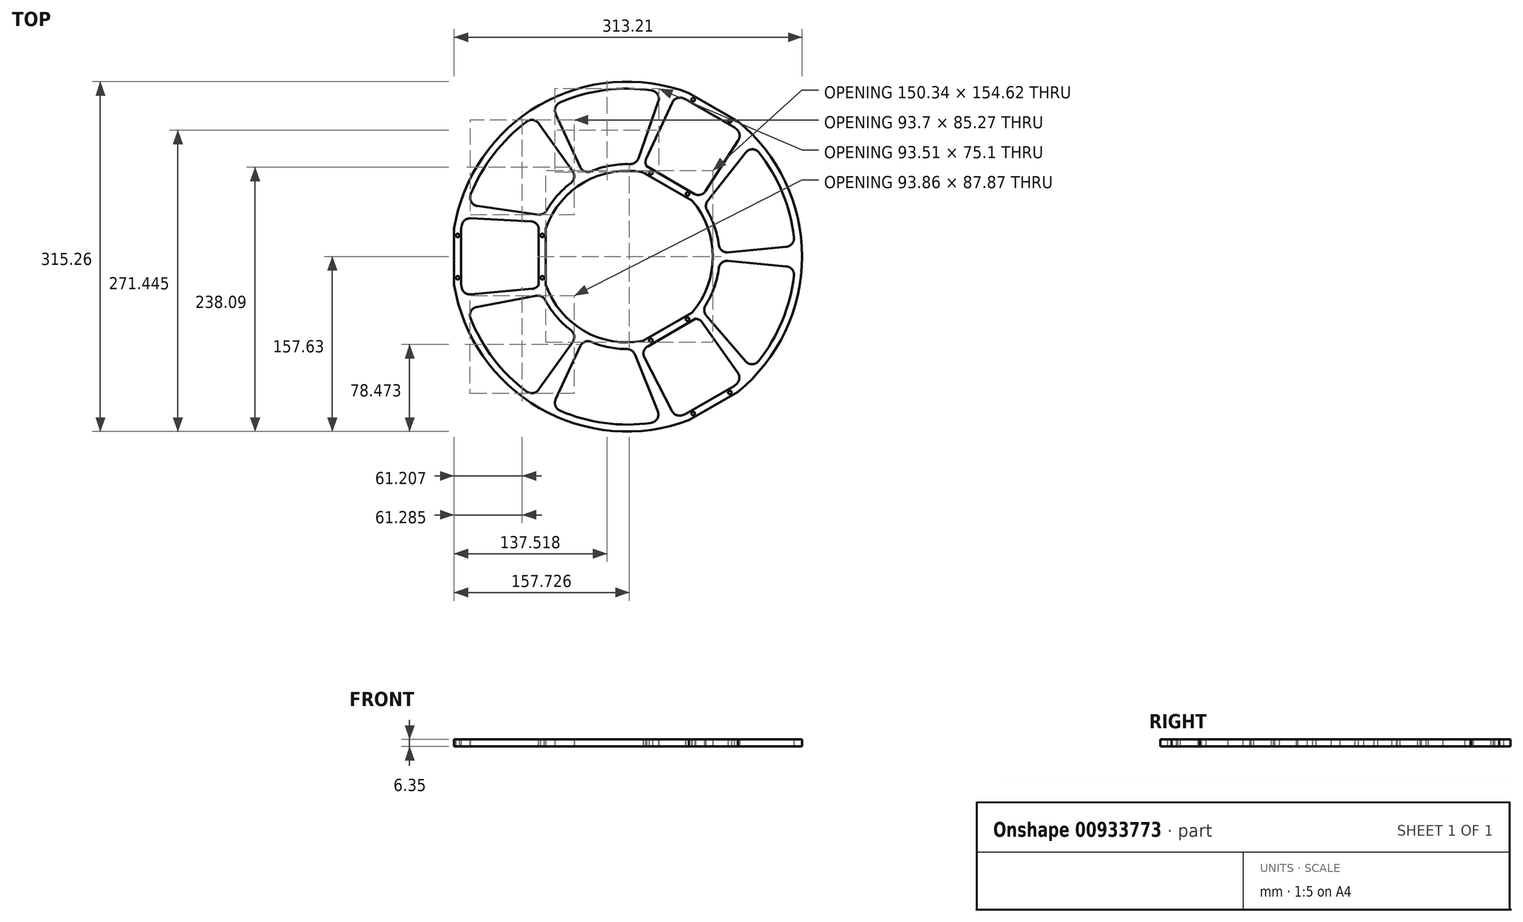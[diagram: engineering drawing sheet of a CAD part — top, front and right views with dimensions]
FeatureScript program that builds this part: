
annotation { "Feature Type Name" : "Feature", "Feature Type Description" : "" }
export const myFeature = defineFeature(function(context is Context, id is Id, definition is map)
    precondition{}
    {
        {
            var Q0;
            Q0=qCreatedBy(makeId("Top.planeOp"),FACE);
            var sketch = newSketch(context, id + "F0", { "sketchPlane" : qUnion([Q0])});
            skLineSegment(sketch, "E0", {"start": v(-79.38, 25.4) * mm, "end": v(-79.38, -25.4) * mm});
            skLineSegment(sketch, "E1", {"start": v(-79.38, -25.4) * mm, "end": v(-73.02, -25.4) * mm});
            skLineSegment(sketch, "E2", {"start": v(-73.02, -25.4) * mm, "end": v(-73.02, 25.4) * mm});
            skLineSegment(sketch, "E3", {"start": v(-73.02, 25.4) * mm, "end": v(-79.38, 25.4) * mm});
            skPoint(sketch, "E4", {"position": v(-79.38, 0) * mm});
            skPoint(sketch, "E5", {"position": v(-76.2, 25.4) * mm});
            skLineSegment(sketch, "E6.bottom", {"start": v(-149.22, 25.4) * mm, "end": v(-155.57, 25.4) * mm});
            skLineSegment(sketch, "E6.top", {"start": v(-149.22, -25.4) * mm, "end": v(-155.57, -25.4) * mm});
            skLineSegment(sketch, "E6.left", {"start": v(-149.22, 25.4) * mm, "end": v(-149.22, -25.4) * mm});
            skLineSegment(sketch, "E6.right", {"start": v(-155.57, 25.4) * mm, "end": v(-155.57, -25.4) * mm});
            skPoint(sketch, "E7", {"position": v(-152.4, 25.4) * mm});
            skCircle(sketch, "E8", {"center": v(0, 0) * mm, "radius": 77.32 * mm, "construction": true});
            skCircle(sketch, "E9", {"center": v(0, 0) * mm, "radius": 83.34 * mm, "construction": true});
            skCircle(sketch, "E10", {"center": v(0, 0) * mm, "radius": 151.37 * mm, "construction": true});
            skCircle(sketch, "E11", {"center": v(0, 0) * mm, "radius": 157.63 * mm, "construction": true});
            skCircle(sketch, "E12", {"center": v(-152.4, 19.05) * mm, "radius": 1.59 * mm});
            skCircle(sketch, "E13", {"center": v(-152.4, -19.05) * mm, "radius": 1.59 * mm});
            skCircle(sketch, "E14", {"center": v(-76.2, -19.05) * mm, "radius": 1.59 * mm});
            skCircle(sketch, "E15", {"center": v(-76.2, 19.05) * mm, "radius": 1.59 * mm});
            skCircle(sketch, "E16", {"center": v(0, 0) * mm, "radius": 33.02 * mm, "construction": true});
            skCircle(sketch, "E17", {"center": v(0, 0) * mm, "radius": 44.45 * mm, "construction": true});
            skSolve(sketch);
        }
        {
            var Q0;
            Q0 = qSketchRegion(id + "F0", true);
            extrude(context, id + "F1", {"entities" : qUnion([Q0]), "depth" : 6.35 * mm, "offsetDistance" : 25.4 * mm});
        }
        {
            var Q0;
            Q0=makeQuery(id+"F1.opExtrude","SWEPT_BODY",BODY,{"disambiguationData":[OSD([sQuery(id+"F0.wireOp",EDGE,"E6.bottom"),sQuery(id+"F0.wireOp",EDGE,"E6.top"),sQuery(id+"F0.wireOp",EDGE,"E6.left"),sQuery(id+"F0.wireOp",EDGE,"E6.right")])]});
            var Q1;
            Q1=makeQuery(id+"F1.opExtrude","SWEPT_BODY",BODY,{"disambiguationData":[OSD([sQuery(id+"F0.wireOp",EDGE,"E0"),sQuery(id+"F0.wireOp",EDGE,"E1"),sQuery(id+"F0.wireOp",EDGE,"E2"),sQuery(id+"F0.wireOp",EDGE,"E3")])]});
            var Q2;
            Q2=sQuery(id+"F0.wireOp",EDGE,"E8");
            circularPattern(context, id + "F2", {"operationType" : NewBodyOperationType.ADD, "entities" : qUnion([Q0, Q1]), "axis" : qUnion([Q2]), "angle" : 360 * degree, "instanceCount" : 3, "equalSpace" : true});
        }
        {
            var Q0;
            Q0=qCreatedBy(makeId("Top.planeOp"),FACE);
            var sketch = newSketch(context, id + "F3", { "sketchPlane" : qUnion([Q0])});
            skArc(sketch, "E18", {"start": v(14.52, 75.94) * mm, "mid": v(-38.66, 66.96) * mm, "end": v(-73.02, 25.4) * mm});
            skArc(sketch, "E19", {"start": v(17.7, 81.44) * mm, "mid": v(-41.67, 72.17) * mm, "end": v(-79.37, 25.4) * mm});
            skArc(sketch, "E20", {"start": v(52.62, 141.93) * mm, "mid": v(-75.69, 131.1) * mm, "end": v(-149.22, 25.4) * mm});
            skArc(sketch, "E21", {"start": v(55.8, 147.43) * mm, "mid": v(-78.82, 136.52) * mm, "end": v(-155.58, 25.4) * mm});
            skLineSegment(sketch, "E22", {"start": v(14.52, 75.94) * mm, "end": v(17.7, 81.44) * mm});
            skLineSegment(sketch, "E23", {"start": v(-73.02, 25.4) * mm, "end": v(-79.37, 25.4) * mm});
            skLineSegment(sketch, "E24", {"start": v(55.8, 147.43) * mm, "end": v(52.62, 141.93) * mm});
            skLineSegment(sketch, "E25", {"start": v(-155.58, 25.4) * mm, "end": v(-149.22, 25.4) * mm});
            skPoint(sketch, "E26", {"position": v(-75.69, 131.1) * mm});
            skPoint(sketch, "E27", {"position": v(-41.67, 72.17) * mm});
            skLineSegment(sketch, "E28", {"start": v(-75.69, 131.1) * mm, "end": v(-41.67, 72.17) * mm, "construction": true});
            skLineSegment(sketch, "E29", {"start": v(-83.78, 126.07) * mm, "end": v(-44.39, 70.53) * mm});
            skLineSegment(sketch, "E30", {"start": v(-38.9, 73.7) * mm, "end": v(-67.3, 135.6) * mm});
            skLineSegment(sketch, "E31", {"start": v(-147.33, 34.74) * mm, "end": v(-77.21, 31.37) * mm});
            skLineSegment(sketch, "E32", {"start": v(-143.9, 46.96) * mm, "end": v(-74.6, 37.16) * mm});
            skLineSegment(sketch, "E33", {"start": v(43.58, 144.96) * mm, "end": v(14.58, 82.06) * mm});
            skLineSegment(sketch, "E34", {"start": v(8.29, 82.93) * mm, "end": v(31.28, 148.1) * mm});
            skSolve(sketch);
        }
        {
            var Q0;
            Q0=makeQuery(id+"F3.imprint","IMPRINT",FACE,{"disambiguationData":[TD([[makeQuery(id+"F3.imprint","IMPRINT",EDGE,{"derivedFrom":sQuery(id+"F3.wireOp",EDGE,"E21")}),1.0]])]});
            var Q1;
            {var subQ0=sQuery(id+"F3.wireOp",EDGE,"E33");Q1=makeQuery(id+"F3.imprint","IMPRINT",FACE,{"disambiguationData":[TD([[makeQuery(id+"F3.imprint","IMPRINT",EDGE,{"derivedFrom":subQ0}),-1.0]])]});}
            var Q2;
            {var subQ0=sQuery(id+"F3.wireOp",EDGE,"E29");Q2=makeQuery(id+"F3.imprint","IMPRINT",FACE,{"disambiguationData":[TD([[makeQuery(id+"F3.imprint","IMPRINT",EDGE,{"derivedFrom":subQ0}),1.0]])]});}
            var Q3;
            {var subQ0=sQuery(id+"F3.wireOp",EDGE,"E31");Q3=makeQuery(id+"F3.imprint","IMPRINT",FACE,{"disambiguationData":[TD([[makeQuery(id+"F3.imprint","IMPRINT",EDGE,{"derivedFrom":subQ0}),1.0]])]});}
            var Q4;
            Q4=makeQuery(id+"F3.imprint","IMPRINT",FACE,{"disambiguationData":[TD([[makeQuery(id+"F3.imprint","IMPRINT",EDGE,{"derivedFrom":sQuery(id+"F3.wireOp",EDGE,"E18")}),-1.0]])]});
            extrude(context, id + "F4", {"entities" : qUnion([Q0, Q1, Q2, Q3, Q4]), "operationType" : NewBodyOperationType.ADD, "depth" : 6.35 * mm, "offsetDistance" : 25.4 * mm});
        }
        {
            var Q0;
            Q0=makeQuery(id+"F4.opExtrude","SWEPT_EDGE",EDGE,{"disambiguationData":[OSD([sQuery(id+"F3.wireOp",EDGE,"E20"),sQuery(id+"F3.wireOp",EDGE,"E29")])]});
            var Q1;
            Q1=makeQuery(id+"F4.opExtrude","SWEPT_EDGE",EDGE,{"disambiguationData":[OSD([sQuery(id+"F3.wireOp",EDGE,"E20"),sQuery(id+"F3.wireOp",EDGE,"E32")])]});
            var Q2;
            Q2=makeQuery(id+"F4.opExtrude","SWEPT_EDGE",EDGE,{"disambiguationData":[OSD([sQuery(id+"F3.wireOp",EDGE,"E19"),sQuery(id+"F3.wireOp",EDGE,"E32")])]});
            var Q3;
            Q3=makeQuery(id+"F4.opExtrude","SWEPT_EDGE",EDGE,{"disambiguationData":[OSD([sQuery(id+"F3.wireOp",EDGE,"E19"),sQuery(id+"F3.wireOp",EDGE,"E29")])]});
            var Q4;
            Q4=makeQuery(id+"F4.opExtrude","SWEPT_EDGE",EDGE,{"disambiguationData":[OSD([sQuery(id+"F3.wireOp",EDGE,"E19"),sQuery(id+"F3.wireOp",EDGE,"E30")])]});
            var Q5;
            Q5=makeQuery(id+"F4.opExtrude","SWEPT_EDGE",EDGE,{"disambiguationData":[OSD([sQuery(id+"F3.wireOp",EDGE,"E19"),sQuery(id+"F3.wireOp",EDGE,"E34")])]});
            var Q6;
            Q6=makeQuery(id+"F4.opExtrude","SWEPT_EDGE",EDGE,{"disambiguationData":[OSD([sQuery(id+"F3.wireOp",EDGE,"E20"),sQuery(id+"F3.wireOp",EDGE,"E34")])]});
            var Q7;
            Q7=makeQuery(id+"F4.opExtrude","SWEPT_EDGE",EDGE,{"disambiguationData":[OSD([sQuery(id+"F3.wireOp",EDGE,"E20"),sQuery(id+"F3.wireOp",EDGE,"E30")])]});
            var Q8;
            Q8=makeQuery(id+"F4.opExtrude","SWEPT_EDGE",EDGE,{"disambiguationData":[OSD([sQuery(id+"F3.wireOp",EDGE,"E20"),sQuery(id+"F3.wireOp",EDGE,"E31")])]});
            var Q9;
            Q9=makeQuery(id+"F4.opExtrude","SWEPT_EDGE",EDGE,{"disambiguationData":[OSD([sQuery(id+"F3.wireOp",EDGE,"E19"),sQuery(id+"F3.wireOp",EDGE,"E31")])]});
            var Q10;
            Q10=makeQuery(id+"F4.opExtrude","SWEPT_EDGE",EDGE,{"disambiguationData":[OSD([sQuery(id+"F3.wireOp",EDGE,"E20"),sQuery(id+"F3.wireOp",EDGE,"E33")])]});
            var Q11;
            Q11=makeQuery(id+"F4.opExtrude","SWEPT_EDGE",EDGE,{"disambiguationData":[OSD([sQuery(id+"F3.wireOp",EDGE,"E19"),sQuery(id+"F3.wireOp",EDGE,"E33")])]});
            fillet(context, id + "F5", {"entities" : qUnion([Q0, Q1, Q2, Q3, Q4, Q5, Q6, Q7, Q8, Q9, Q10, Q11]), "radius" : 7.62 * mm, "tangentPropagation" : true, "allowEdgeOverflow" : false});
        }
        {
            var Q0;
            Q0=makeQuery(id+"F5.opFillet","BLEND_EDGE",EDGE,{"blendedFrom":[makeQuery(id+"F4.opExtrude","SWEPT_EDGE",EDGE,{"disambiguationData":[OSD([sQuery(id+"F3.wireOp",EDGE,"E19"),sQuery(id+"F3.wireOp",EDGE,"E33")])]}),makeQuery(id+"F2.opPattern","COPY",FACE,{"derivedFrom":makeQuery(id+"F1.opExtrude","SWEPT_FACE",FACE,{"disambiguationData":[OSD([sQuery(id+"F0.wireOp",EDGE,"E0")])]}),"instanceName":"5"})],"blendedInto":[makeQuery(id+"F2.opPattern","COPY",FACE,{"derivedFrom":makeQuery(id+"F1.opExtrude","SWEPT_FACE",FACE,{"disambiguationData":[OSD([sQuery(id+"F0.wireOp",EDGE,"E0")])]}),"instanceName":"5"})]});
            var Q1;
            Q1=makeQuery(id+"F5.opFillet","BLEND_EDGE",EDGE,{"blendedFrom":[makeQuery(id+"F4.opExtrude","SWEPT_EDGE",EDGE,{"disambiguationData":[OSD([sQuery(id+"F3.wireOp",EDGE,"E20"),sQuery(id+"F3.wireOp",EDGE,"E33")])]}),makeQuery(id+"F2.opPattern","COPY",FACE,{"derivedFrom":makeQuery(id+"F1.opExtrude","SWEPT_FACE",FACE,{"disambiguationData":[OSD([sQuery(id+"F0.wireOp",EDGE,"E6.left")])]}),"instanceName":"5"})],"blendedInto":[makeQuery(id+"F2.opPattern","COPY",FACE,{"derivedFrom":makeQuery(id+"F1.opExtrude","SWEPT_FACE",FACE,{"disambiguationData":[OSD([sQuery(id+"F0.wireOp",EDGE,"E6.left")])]}),"instanceName":"5"})]});
            var Q2;
            Q2=makeQuery(id+"F5.opFillet","BLEND_EDGE",EDGE,{"blendedFrom":[makeQuery(id+"F4.opExtrude","SWEPT_EDGE",EDGE,{"disambiguationData":[OSD([sQuery(id+"F3.wireOp",EDGE,"E19"),sQuery(id+"F3.wireOp",EDGE,"E31")])]}),makeQuery(id+"F1.opExtrude","SWEPT_FACE",FACE,{"disambiguationData":[OSD([sQuery(id+"F0.wireOp",EDGE,"E0")])]})],"blendedInto":[makeQuery(id+"F1.opExtrude","SWEPT_FACE",FACE,{"disambiguationData":[OSD([sQuery(id+"F0.wireOp",EDGE,"E0")])]})]});
            var Q3;
            Q3=makeQuery(id+"F5.opFillet","BLEND_EDGE",EDGE,{"blendedFrom":[makeQuery(id+"F4.opExtrude","SWEPT_EDGE",EDGE,{"disambiguationData":[OSD([sQuery(id+"F3.wireOp",EDGE,"E20"),sQuery(id+"F3.wireOp",EDGE,"E31")])]}),makeQuery(id+"F1.opExtrude","SWEPT_FACE",FACE,{"disambiguationData":[OSD([sQuery(id+"F0.wireOp",EDGE,"E6.left")])]})],"blendedInto":[makeQuery(id+"F1.opExtrude","SWEPT_FACE",FACE,{"disambiguationData":[OSD([sQuery(id+"F0.wireOp",EDGE,"E6.left")])]})]});
            var Q4;
            {var subQ0=sQuery(id+"F3.wireOp",EDGE,"E19");Q4=makeQuery(id+"F5.opFillet","BLEND_EDGE",EDGE,{"blendedFrom":[makeQuery(id+"F4.opExtrude","SWEPT_EDGE",EDGE,{"disambiguationData":[OSD([subQ0,sQuery(id+"F3.wireOp",EDGE,"E29")])]}),makeQuery(id+"F4.opExtrude","SWEPT_EDGE",EDGE,{"disambiguationData":[OSD([subQ0,sQuery(id+"F3.wireOp",EDGE,"E32")])]})],"blendedInto":[]});}
            var Q5;
            {var subQ0=sQuery(id+"F3.wireOp",EDGE,"E19");Q5=makeQuery(id+"F5.opFillet","BLEND_EDGE",EDGE,{"blendedFrom":[makeQuery(id+"F4.opExtrude","SWEPT_EDGE",EDGE,{"disambiguationData":[OSD([subQ0,sQuery(id+"F3.wireOp",EDGE,"E30")])]}),makeQuery(id+"F4.opExtrude","SWEPT_EDGE",EDGE,{"disambiguationData":[OSD([subQ0,sQuery(id+"F3.wireOp",EDGE,"E34")])]})],"blendedInto":[]});}
            fillet(context, id + "F6", {"entities" : qUnion([Q0, Q1, Q2, Q3, Q4, Q5]), "radius" : 5.08 * mm, "tangentPropagation" : true, "allowEdgeOverflow" : false});
        }
        {
            var Q0;
            Q0=makeQuery(id+"F1.opExtrude","SWEPT_BODY",BODY,{"disambiguationData":[OSD([sQuery(id+"F0.wireOp",EDGE,"E0"),sQuery(id+"F0.wireOp",EDGE,"E1"),sQuery(id+"F0.wireOp",EDGE,"E2"),sQuery(id+"F0.wireOp",EDGE,"E3")])]});
            var Q1;
            Q1=sQuery(id+"F0.wireOp",EDGE,"E8");
            circularPattern(context, id + "F7", {"operationType" : NewBodyOperationType.ADD, "entities" : qUnion([Q0]), "axis" : qUnion([Q1]), "angle" : 360 * degree, "instanceCount" : 3, "equalSpace" : true});
        }
    });
